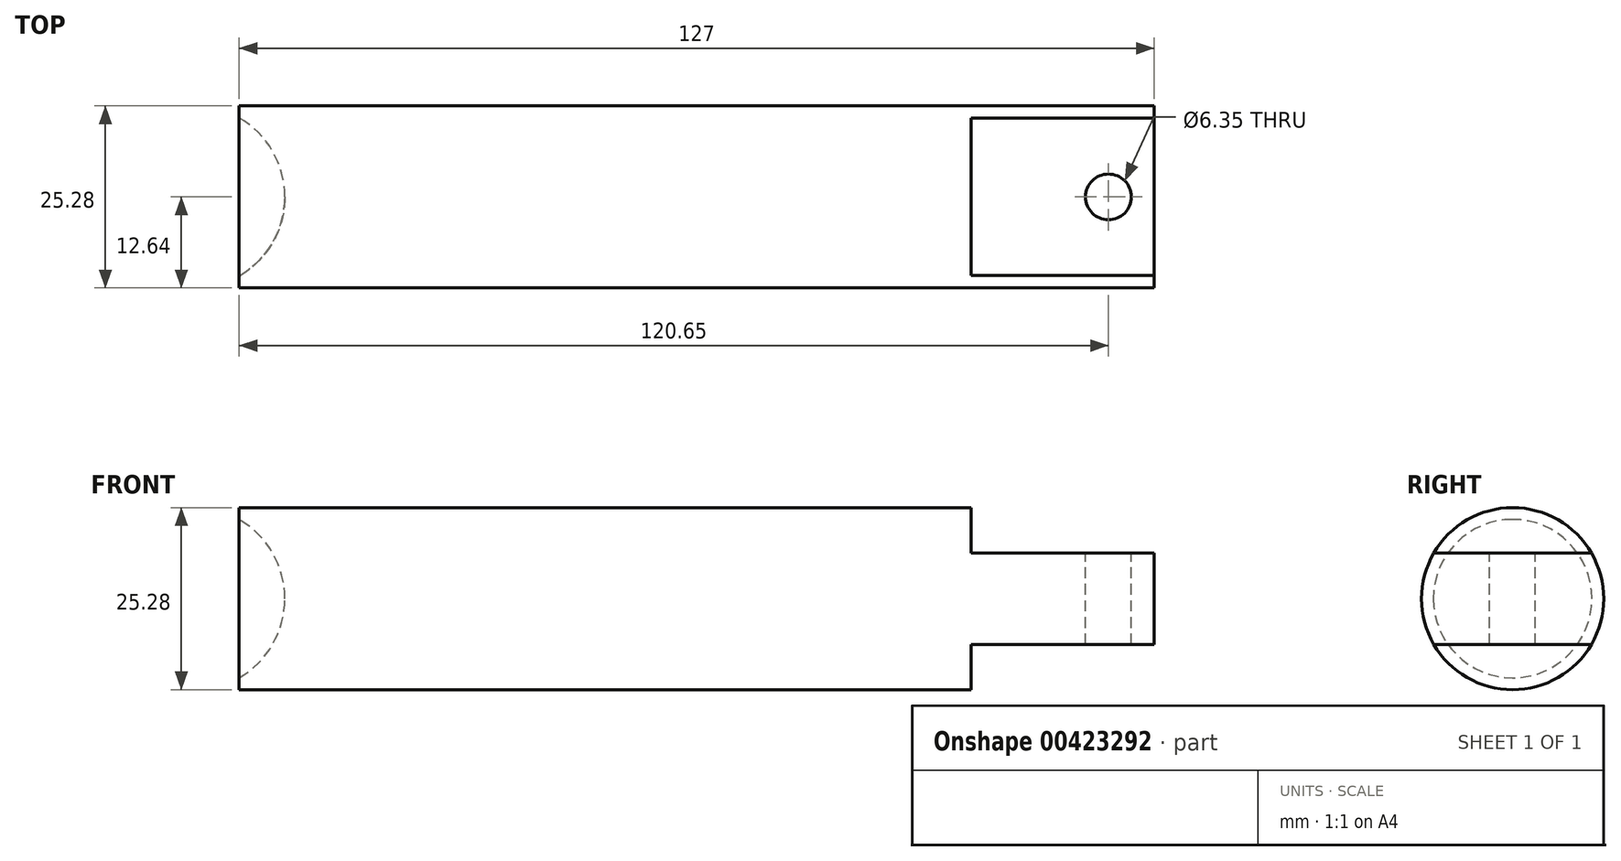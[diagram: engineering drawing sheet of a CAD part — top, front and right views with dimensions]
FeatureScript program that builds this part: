
annotation { "Feature Type Name" : "Feature", "Feature Type Description" : "" }
export const myFeature = defineFeature(function(context is Context, id is Id, definition is map)
    precondition{}
    {
        {
            var Q0;
            Q0=qCreatedBy(makeId("Right.planeOp"),FACE);
            var sketch = newSketch(context, id + "F0", { "sketchPlane" : qUnion([Q0])});
            skCircle(sketch, "E0", {"center": v(0, 0) * mm, "radius": 12.64 * mm});
            skSolve(sketch);
        }
        {
            var Q0;
            Q0 = qSketchRegion(id + "F0", true);
            extrude(context, id + "F1", {"entities" : qUnion([Q0]), "endBound" : BoundingType.SYMMETRIC, "depth" : 127 * mm});
        }
        {
            var Q0;
            Q0=qCreatedBy(makeId("Front.planeOp"),FACE);
            var sketch = newSketch(context, id + "F2", { "sketchPlane" : qUnion([Q0])});
            skLineSegment(sketch, "E1.bottom", {"start": v(86.12, 6.35) * mm, "end": v(38.1, 6.35) * mm});
            skLineSegment(sketch, "E1.top", {"start": v(86.12, 27.57) * mm, "end": v(38.1, 27.57) * mm});
            skLineSegment(sketch, "E1.left", {"start": v(86.12, 6.35) * mm, "end": v(86.12, 27.57) * mm});
            skLineSegment(sketch, "E1.right", {"start": v(38.1, 6.35) * mm, "end": v(38.1, 27.57) * mm});
            skLineSegment(sketch, "E2.bottom", {"start": v(86.12, -6.35) * mm, "end": v(38.1, -6.35) * mm});
            skLineSegment(sketch, "E2.top", {"start": v(86.12, -27.57) * mm, "end": v(38.1, -27.57) * mm});
            skLineSegment(sketch, "E2.left", {"start": v(86.12, -6.35) * mm, "end": v(86.12, -27.57) * mm});
            skLineSegment(sketch, "E2.right", {"start": v(38.1, -6.35) * mm, "end": v(38.1, -27.57) * mm});
            skSolve(sketch);
        }
        {
            var Q0;
            Q0 = qSketchRegion(id + "F2", true);
            extrude(context, id + "F3", {"entities" : qUnion([Q0]), "operationType" : NewBodyOperationType.REMOVE, "endBound" : BoundingType.SYMMETRIC, "oppositeDirection" : true, "depth" : 508 * mm});
        }
        {
            var Q0;
            Q0=makeQuery(id+"F3.boolean.opBoolean","COPY",FACE,{"derivedFrom":makeQuery(id+"F3.opExtrude","SWEPT_FACE",FACE,{"disambiguationData":[OSD([sQuery(id+"F2.wireOp",EDGE,"E1.bottom")])]})});
            var sketch = newSketch(context, id + "F4", { "sketchPlane" : qUnion([Q0])});
            skCircle(sketch, "E3", {"center": v(57.15, 0) * mm, "radius": 3.18 * mm});
            skSolve(sketch);
        }
        {
            var Q0;
            Q0 = qSketchRegion(id + "F4", true);
            extrude(context, id + "F5", {"entities" : qUnion([Q0]), "operationType" : NewBodyOperationType.REMOVE, "endBound" : BoundingType.THROUGH_ALL, "oppositeDirection" : true, "depth" : 25.4 * mm});
        }
        {
            var Q0;
            Q0=qCreatedBy(makeId("Top.planeOp"),FACE);
            var sketch = newSketch(context, id + "F6", { "sketchPlane" : qUnion([Q0])});
            skArc(sketch, "E4", {"start": v(-57.15, 0) * mm, "mid": v(-58.85, 6.35) * mm, "end": v(-63.5, 11) * mm});
            skLineSegment(sketch, "E5", {"start": v(-63.5, 12.64) * mm, "end": v(63.5, 12.64) * mm});
            skLineSegment(sketch, "E6", {"start": v(63.5, -12.64) * mm, "end": v(-63.5, -12.64) * mm});
            skLineSegment(sketch, "E7", {"start": v(-57.15, 0) * mm, "end": v(-63.5, 0) * mm});
            skLineSegment(sketch, "E8", {"start": v(-63.5, 11) * mm, "end": v(-63.5, 0) * mm});
            skSolve(sketch);
        }
        {
            var Q0;
            Q0 = qSketchRegion(id + "F6", true);
            var Q1;
            Q1=sQuery(id+"F6.wireOp",EDGE,"E7");
            revolve(context, id + "F7", {"operationType" : NewBodyOperationType.REMOVE, "entities" : qUnion([Q0]), "axis" : qUnion([Q1]), "revolveType" : RevolveType.FULL, "oppositeDirection" : true});
        }
    });
